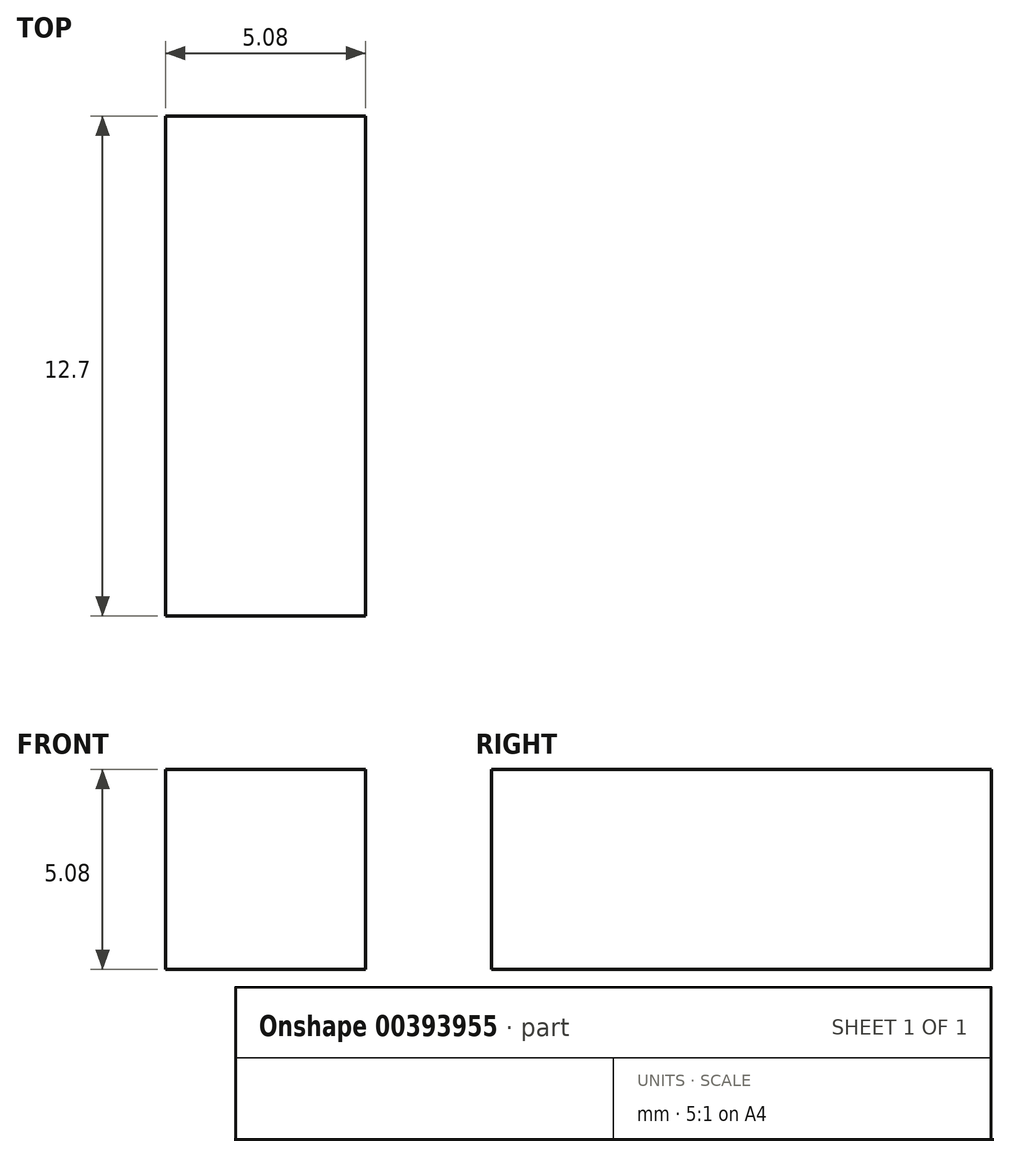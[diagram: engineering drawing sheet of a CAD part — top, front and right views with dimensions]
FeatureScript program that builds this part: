
annotation { "Feature Type Name" : "Feature", "Feature Type Description" : "" }
export const myFeature = defineFeature(function(context is Context, id is Id, definition is map)
    precondition{}
    {
        {
            var Q0;
            Q0=qCreatedBy(makeId("Front.planeOp"),FACE);
            var sketch = newSketch(context, id + "F0", { "sketchPlane" : qUnion([Q0])});
            skLineSegment(sketch, "E0.bottom", {"start": v(0, 0) * mm, "end": v(5.08, 0) * mm});
            skLineSegment(sketch, "E0.top", {"start": v(0, 5.08) * mm, "end": v(5.08, 5.08) * mm});
            skLineSegment(sketch, "E0.left", {"start": v(0, 0) * mm, "end": v(0, 5.08) * mm});
            skLineSegment(sketch, "E0.right", {"start": v(5.08, 0) * mm, "end": v(5.08, 5.08) * mm});
            skSolve(sketch);
        }
        {
            var Q0;
            Q0 = qSketchRegion(id + "F0", true);
            extrude(context, id + "F1", {"entities" : qUnion([Q0]), "depth" : 12.7 * mm});
        }
    });
